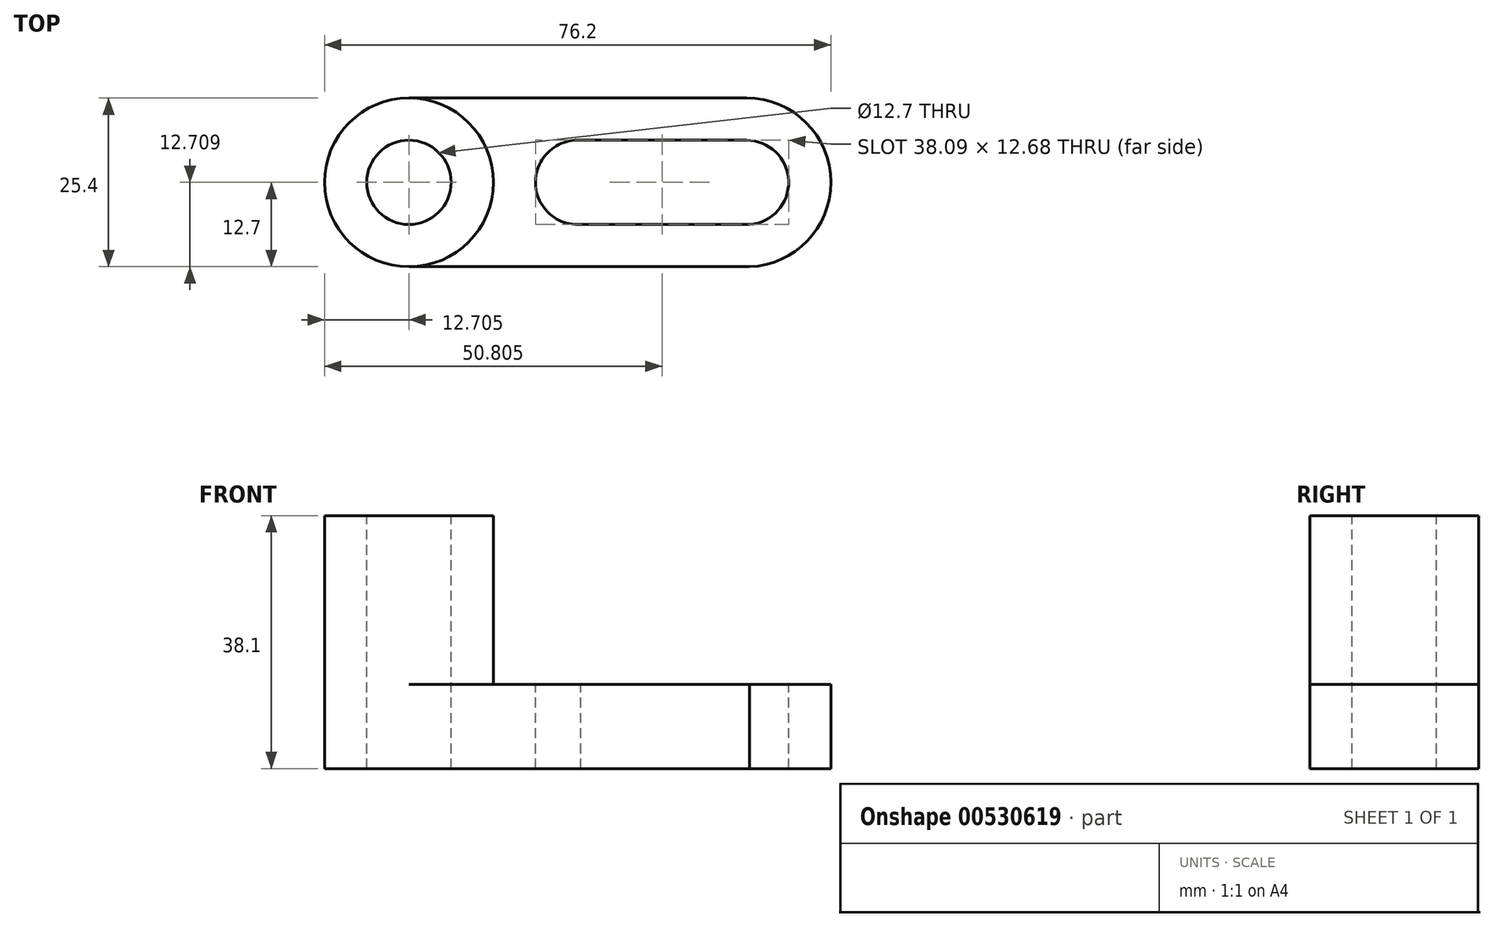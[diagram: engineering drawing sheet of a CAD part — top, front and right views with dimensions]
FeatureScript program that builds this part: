
annotation { "Feature Type Name" : "Feature", "Feature Type Description" : "" }
export const myFeature = defineFeature(function(context is Context, id is Id, definition is map)
    precondition{}
    {
        {
            var Q0;
            Q0=qCreatedBy(makeId("Front.planeOp"),FACE);
            var sketch = newSketch(context, id + "F0", { "sketchPlane" : qUnion([Q0])});
            skLineSegment(sketch, "E0", {"start": v(-81.29, 39.9) * mm, "end": v(-81.29, 27.2) * mm});
            skLineSegment(sketch, "E1", {"start": v(-5.09, 27.2) * mm, "end": v(-81.29, 27.2) * mm});
            skLineSegment(sketch, "E2", {"start": v(-81.29, 39.9) * mm, "end": v(-5.09, 39.9) * mm});
            skLineSegment(sketch, "E3", {"start": v(-5.09, 39.9) * mm, "end": v(-5.09, 27.2) * mm});
            skSolve(sketch);
        }
        {
            var Q0;
            Q0=makeQuery(id+"F0.imprint","IMPRINT",FACE,{"disambiguationData":[TD([[makeQuery(id+"F0.imprint","IMPRINT",EDGE,{"derivedFrom":sQuery(id+"F0.wireOp",EDGE,"E0")}),1.0]])]});
            extrude(context, id + "F1", {"entities" : qUnion([Q0]), "depth" : 25.4 * mm, "offsetDistance" : 25.4 * mm});
        }
        {
            var Q0;
            Q0=makeQuery(id+"F1.opExtrude","SWEPT_FACE",FACE,{"disambiguationData":[OSD([sQuery(id+"F0.wireOp",EDGE,"E2")])]});
            var sketch = newSketch(context, id + "F2", { "sketchPlane" : qUnion([Q0])});
            skLineSegment(sketch, "E4", {"start": v(-81.29, 0) * mm, "end": v(-81.29, -25.4) * mm});
            skLineSegment(sketch, "E5", {"start": v(-81.29, -25.4) * mm, "end": v(-55.89, -25.4) * mm});
            skLineSegment(sketch, "E6", {"start": v(-55.89, -25.4) * mm, "end": v(-55.89, 0) * mm});
            skLineSegment(sketch, "E7", {"start": v(-55.89, 0) * mm, "end": v(-81.29, 0) * mm});
            skSolve(sketch);
        }
        {
            var Q0;
            Q0=makeQuery(id+"F2.imprint","IMPRINT",FACE,{"disambiguationData":[TD([[makeQuery(id+"F2.imprint","IMPRINT",EDGE,{"derivedFrom":sQuery(id+"F2.wireOp",EDGE,"E4")}),-1.0]])]});
            extrude(context, id + "F3", {"entities" : qUnion([Q0]), "operationType" : NewBodyOperationType.ADD, "depth" : 25.4 * mm, "offsetDistance" : 25.4 * mm});
        }
        {
            var Q0;
            Q0=makeQuery(id+"F3.opExtrude","CAP_FACE",FACE,{"disambiguationData":[OSD([sQuery(id+"F2.wireOp",EDGE,"E4"),sQuery(id+"F2.wireOp",EDGE,"E5"),sQuery(id+"F2.wireOp",EDGE,"E6"),sQuery(id+"F2.wireOp",EDGE,"E7")])],"isStart":false});
            var sketch = newSketch(context, id + "F4", { "sketchPlane" : qUnion([Q0])});
            skLineSegment(sketch, "E8", {"start": v(-68.59, 0) * mm, "end": v(-68.59, -25.4) * mm});
            skCircle(sketch, "E9", {"center": v(-68.59, -12.7) * mm, "radius": 6.35 * mm});
            skLineSegment(sketch, "E10", {"start": v(-81.29, 0) * mm, "end": v(-81.29, -12.7) * mm});
            skArc(sketch, "E11", {"start": v(-68.59, 0) * mm, "mid": v(-77.57, -3.72) * mm, "end": v(-81.29, -12.7) * mm});
            skArc(sketch, "E12", {"start": v(-55.89, -12.7) * mm, "mid": v(-59.6, -3.72) * mm, "end": v(-68.59, 0) * mm});
            skArc(sketch, "E13", {"start": v(-81.29, -12.7) * mm, "mid": v(-77.57, -21.68) * mm, "end": v(-68.59, -25.4) * mm});
            skArc(sketch, "E14", {"start": v(-68.59, -25.4) * mm, "mid": v(-59.6, -21.68) * mm, "end": v(-55.89, -12.7) * mm});
            skLineSegment(sketch, "E15", {"start": v(-55.89, -12.7) * mm, "end": v(-36.84, -12.7) * mm});
            skLineSegment(sketch, "E16", {"start": v(-5.09, -12.7) * mm, "end": v(-11.44, -12.7) * mm});
            skLineSegment(sketch, "E17", {"start": v(-55.89, -12.7) * mm, "end": v(-49.54, -12.7) * mm});
            skLineSegment(sketch, "E18", {"start": v(-49.54, -12.7) * mm, "end": v(-43.19, -12.7) * mm});
            skLineSegment(sketch, "E19", {"start": v(-11.44, -12.7) * mm, "end": v(-17.79, -12.7) * mm});
            skArc(sketch, "E20", {"start": v(-17.32, -19.03) * mm, "mid": v(-11.44, -12.47) * mm, "end": v(-17.79, -6.35) * mm});
            skCircle(sketch, "E21", {"center": v(-43.19, -12.7) * mm, "radius": 6.35 * mm});
            skLineSegment(sketch, "E22", {"start": v(-43.19, -6.35) * mm, "end": v(-17.79, -6.35) * mm});
            skLineSegment(sketch, "E23", {"start": v(-42.72, -19.03) * mm, "end": v(-17.32, -19.03) * mm});
            skLineSegment(sketch, "E24", {"start": v(-17.32, -19.03) * mm, "end": v(-42.72, -19.03) * mm});
            skLineSegment(sketch, "E25", {"start": v(-17.76, -26.11) * mm, "end": v(-5.06, -26.11) * mm});
            skPoint(sketch, "E26.start.orphan", {"position": v(-5.56, 0) * mm});
            skLineSegment(sketch, "E27", {"start": v(-17.79, -6.35) * mm, "end": v(-17.79, 0) * mm});
            skArc(sketch, "E28", {"start": v(-5.09, -12.7) * mm, "mid": v(-8.8, -3.72) * mm, "end": v(-17.79, 0) * mm});
            skLineSegment(sketch, "E29", {"start": v(-5.06, -26.11) * mm, "end": v(-17.76, -26.11) * mm});
            skLineSegment(sketch, "E30", {"start": v(-17.79, 0) * mm, "end": v(-17.79, -6.35) * mm});
            skLineSegment(sketch, "E31", {"start": v(-17.78, -19.05) * mm, "end": v(-17.78, -19.03) * mm});
            skArc(sketch, "E32", {"start": v(-17.76, -26.11) * mm, "mid": v(-8.54, -22.14) * mm, "end": v(-5.09, -12.7) * mm});
            skLineSegment(sketch, "E33.trimOffspring", {"start": v(-17.79, -12.7) * mm, "end": v(-5.09, -12.7) * mm});
            skSolve(sketch);
        }
        {
            var Q0;
            {var subQ0=sQuery(id+"F4.wireOp",EDGE,"E10");Q0=makeQuery(id+"F4.imprint","IMPRINT",FACE,{"disambiguationData":[TD([[makeQuery(id+"F4.imprint","IMPRINT",EDGE,{"derivedFrom":subQ0}),-1.0]])]});}
            var Q1;
            {var subQ0=sQuery(id+"F4.wireOp",EDGE,"E13");Q1=makeQuery(id+"F4.imprint","IMPRINT",FACE,{"disambiguationData":[TD([[makeQuery(id+"F4.imprint","IMPRINT",EDGE,{"derivedFrom":subQ0}),-1.0]])]});}
            var Q2;
            {var subQ0=sQuery(id+"F4.wireOp",EDGE,"E9");var subQ1=sQuery(id+"F4.wireOp",EDGE,"E8");var subQ2=makeQuery(id+"F4.imprint","INTERSECT",VERTEX,{"disambiguationData":[OD(0.0)],"derivedFrom":[subQ1,subQ0]});Q2=makeQuery(id+"F4.imprint","IMPRINT",FACE,{"disambiguationData":[TD([[makeQuery(id+"F4.imprint","IMPRINT",EDGE,{"disambiguationData":[TD([[subQ2,-1.0]])],"derivedFrom":subQ1}),-1.0]])]});}
            var Q3;
            {var subQ0=sQuery(id+"F4.wireOp",EDGE,"E9");var subQ1=sQuery(id+"F4.wireOp",EDGE,"E8");var subQ2=makeQuery(id+"F4.imprint","INTERSECT",VERTEX,{"disambiguationData":[OD(0.0)],"derivedFrom":[subQ1,subQ0]});Q3=makeQuery(id+"F4.imprint","IMPRINT",FACE,{"disambiguationData":[TD([[makeQuery(id+"F4.imprint","IMPRINT",EDGE,{"disambiguationData":[TD([[subQ2,-1.0]])],"derivedFrom":subQ1}),1.0]])]});}
            var Q4;
            {var subQ0=sQuery(id+"F4.wireOp",EDGE,"E15");Q4=makeQuery(id+"F4.imprint","IMPRINT",FACE,{"disambiguationData":[TD([[makeQuery(id+"F4.imprint","IMPRINT",EDGE,{"derivedFrom":subQ0}),-1.0]])]});}
            var Q5;
            {var subQ0=sQuery(id+"F4.wireOp",EDGE,"E15");Q5=makeQuery(id+"F4.imprint","IMPRINT",FACE,{"disambiguationData":[TD([[makeQuery(id+"F4.imprint","IMPRINT",EDGE,{"derivedFrom":subQ0}),1.0]])]});}
            var Q6;
            {var subQ2=sQuery(id+"F4.wireOp",EDGE,"E22");Q6=makeQuery(id+"F4.imprint","IMPRINT",FACE,{"disambiguationData":[TD([[makeQuery(id+"F4.imprint","IMPRINT",EDGE,{"derivedFrom":subQ2}),-1.0]])]});}
            extrude(context, id + "F5", {"entities" : qUnion([Q0, Q1, Q2, Q3, Q4, Q5, Q6]), "operationType" : NewBodyOperationType.REMOVE, "endBound" : BoundingType.THROUGH_ALL, "oppositeDirection" : true, "depth" : 25.4 * mm, "offsetDistance" : 25.4 * mm});
        }
        {
            var Q0;
            Q0=makeQuery(id+"F1.opExtrude","SWEPT_FACE",FACE,{"disambiguationData":[OSD([sQuery(id+"F0.wireOp",EDGE,"E2")])]});
            var sketch = newSketch(context, id + "F6", { "sketchPlane" : qUnion([Q0])});
            skLineSegment(sketch, "E34", {"start": v(-17.79, -6.35) * mm, "end": v(-17.79, 0) * mm});
            skLineSegment(sketch, "E35", {"start": v(-17.79, 0) * mm, "end": v(-17.32, -25.4) * mm});
            skArc(sketch, "E36", {"start": v(-5.09, -12.7) * mm, "mid": v(-8.8, -3.72) * mm, "end": v(-17.79, 0) * mm});
            skArc(sketch, "E37", {"start": v(-17.32, -25.4) * mm, "mid": v(-8.64, -21.52) * mm, "end": v(-5.09, -12.7) * mm});
            skLineSegment(sketch, "E38", {"start": v(-55.89, -12.7) * mm, "end": v(-68.59, -12.7) * mm});
            skLineSegment(sketch, "E39", {"start": v(-68.59, -12.7) * mm, "end": v(-68.59, 0) * mm});
            skLineSegment(sketch, "E40", {"start": v(-68.59, 0) * mm, "end": v(-68.59, -25.4) * mm});
            skArc(sketch, "E41", {"start": v(-55.89, -12.7) * mm, "mid": v(-59.6, -3.72) * mm, "end": v(-68.59, 0) * mm});
            skArc(sketch, "E42", {"start": v(-68.59, -25.4) * mm, "mid": v(-59.6, -21.68) * mm, "end": v(-55.89, -12.7) * mm});
            skSolve(sketch);
        }
        {
            var Q0;
            {var subQ0=sQuery(id+"F6.wireOp",EDGE,"E36");Q0=makeQuery(id+"F6.imprint","IMPRINT",FACE,{"disambiguationData":[TD([[makeQuery(id+"F6.imprint","IMPRINT",EDGE,{"derivedFrom":subQ0}),-1.0]])]});}
            var Q1;
            {var subQ0=sQuery(id+"F6.wireOp",EDGE,"E37");var subQ1=sQuery(id+"F0.wireOp",EDGE,"E2");var subQ2=makeQuery(id+"F1.opExtrude","CAP_EDGE",EDGE,{"disambiguationData":[OSD([subQ1])],"isStart":false});var subQ3=makeQuery(id+"F6.imprint","INTERSECT",VERTEX,{"derivedFrom":[subQ2,sQuery(id+"F6.wireOp",EDGE,"E35"),subQ0]});Q1=makeQuery(id+"F6.imprint","IMPRINT",FACE,{"disambiguationData":[TD([[makeQuery(id+"F6.imprint","IMPRINT",EDGE,{"disambiguationData":[TD([[subQ3,-1.0]])],"derivedFrom":subQ0}),-1.0]])]});}
            extrude(context, id + "F7", {"entities" : qUnion([Q0, Q1]), "operationType" : NewBodyOperationType.REMOVE, "oppositeDirection" : true, "depth" : 25.4 * mm, "offsetDistance" : 25.4 * mm});
        }
        {
            var Q0;
            Q0=makeQuery(id+"F3.opExtrude","CAP_FACE",FACE,{"disambiguationData":[OSD([sQuery(id+"F2.wireOp",EDGE,"E4"),sQuery(id+"F2.wireOp",EDGE,"E5"),sQuery(id+"F2.wireOp",EDGE,"E6"),sQuery(id+"F2.wireOp",EDGE,"E7")])],"isStart":false});
            var sketch = newSketch(context, id + "F8", { "sketchPlane" : qUnion([Q0])});
            skLineSegment(sketch, "E43", {"start": v(-68.59, 0) * mm, "end": v(-68.59, -25.4) * mm});
            skArc(sketch, "E44", {"start": v(-55.89, -12.7) * mm, "mid": v(-59.6, -3.72) * mm, "end": v(-68.59, 0) * mm});
            skArc(sketch, "E45", {"start": v(-68.59, -25.4) * mm, "mid": v(-59.6, -21.68) * mm, "end": v(-55.89, -12.7) * mm});
            skSolve(sketch);
        }
        {
            var Q0;
            {var subQ0=sQuery(id+"F8.wireOp",EDGE,"E44");Q0=makeQuery(id+"F8.imprint","IMPRINT",FACE,{"disambiguationData":[TD([[makeQuery(id+"F8.imprint","IMPRINT",EDGE,{"derivedFrom":subQ0}),-1.0]])]});}
            var Q1;
            {var subQ0=sQuery(id+"F8.wireOp",EDGE,"E45");Q1=makeQuery(id+"F8.imprint","IMPRINT",FACE,{"disambiguationData":[TD([[makeQuery(id+"F8.imprint","IMPRINT",EDGE,{"derivedFrom":subQ0}),-1.0]])]});}
            extrude(context, id + "F9", {"entities" : qUnion([Q0, Q1]), "operationType" : NewBodyOperationType.REMOVE, "oppositeDirection" : true, "depth" : 25.4 * mm, "offsetDistance" : 25.4 * mm});
        }
    });
